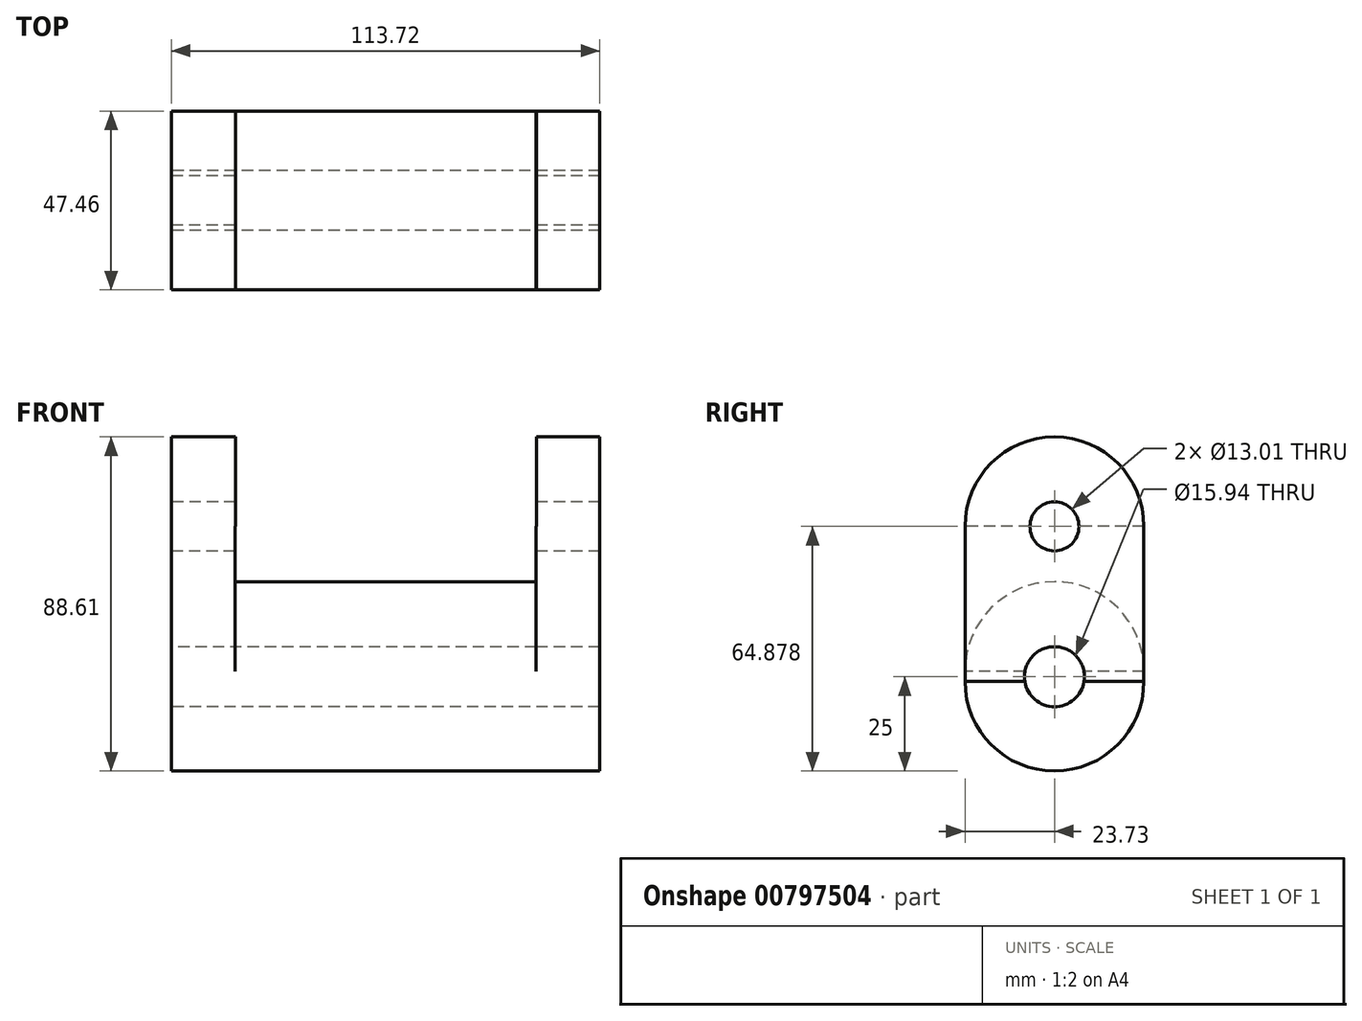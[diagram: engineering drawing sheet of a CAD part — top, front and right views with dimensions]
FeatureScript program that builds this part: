
annotation { "Feature Type Name" : "Feature", "Feature Type Description" : "" }
export const myFeature = defineFeature(function(context is Context, id is Id, definition is map)
    precondition{}
    {
        {
            var Q0;
            Q0=qCreatedBy(makeId("Top.planeOp"),FACE);
            var sketch = newSketch(context, id + "F0", { "sketchPlane" : qUnion([Q0])});
            skLineSegment(sketch, "E0.bottom", {"start": v(39.5, 23.73) * mm, "end": v(-39.5, 23.73) * mm});
            skLineSegment(sketch, "E0.top", {"start": v(39.5, -23.73) * mm, "end": v(-39.5, -23.73) * mm});
            skLineSegment(sketch, "E0.left", {"start": v(39.5, 23.73) * mm, "end": v(39.5, -23.73) * mm});
            skLineSegment(sketch, "E0.right", {"start": v(-39.5, 23.73) * mm, "end": v(-39.5, -23.73) * mm});
            skPoint(sketch, "E0.middle", {"position": v(0, 0) * mm});
            skLineSegment(sketch, "E1.bottom", {"start": v(-39.5, 0) * mm, "end": v(-56.86, 0) * mm});
            skLineSegment(sketch, "E1.top", {"start": v(-39.5, 23.73) * mm, "end": v(-56.86, 23.73) * mm});
            skLineSegment(sketch, "E1.left", {"start": v(-39.5, 0) * mm, "end": v(-39.5, 23.73) * mm});
            skLineSegment(sketch, "E1.right", {"start": v(-56.86, 0) * mm, "end": v(-56.86, 23.73) * mm});
            skLineSegment(sketch, "E2.bottom", {"start": v(-56.86, 0) * mm, "end": v(-39.5, 0) * mm});
            skLineSegment(sketch, "E2.top", {"start": v(-56.86, -23.73) * mm, "end": v(-39.5, -23.73) * mm});
            skLineSegment(sketch, "E2.left", {"start": v(-56.86, 0) * mm, "end": v(-56.86, -23.73) * mm});
            skLineSegment(sketch, "E2.right", {"start": v(-39.5, 0) * mm, "end": v(-39.5, -23.73) * mm});
            skLineSegment(sketch, "E3.bottom", {"start": v(39.5, 23.73) * mm, "end": v(56.86, 23.73) * mm});
            skLineSegment(sketch, "E3.top", {"start": v(39.5, 0) * mm, "end": v(56.86, 0) * mm});
            skLineSegment(sketch, "E3.left", {"start": v(39.5, 23.73) * mm, "end": v(39.5, 0) * mm});
            skLineSegment(sketch, "E3.right", {"start": v(56.86, 23.73) * mm, "end": v(56.86, 0) * mm});
            skLineSegment(sketch, "E4.bottom", {"start": v(56.86, 0) * mm, "end": v(39.5, 0) * mm});
            skLineSegment(sketch, "E4.top", {"start": v(56.86, -23.73) * mm, "end": v(39.5, -23.73) * mm});
            skLineSegment(sketch, "E4.left", {"start": v(56.86, 0) * mm, "end": v(56.86, -23.73) * mm});
            skLineSegment(sketch, "E4.right", {"start": v(39.5, 0) * mm, "end": v(39.5, -23.73) * mm});
            skSolve(sketch);
        }
        {
            var Q0;
            {var subQ2=sQuery(id+"F0.wireOp",EDGE,"E1.bottom");Q0=makeQuery(id+"F0.imprint","IMPRINT",FACE,{"disambiguationData":[TD([[makeQuery(id+"F0.imprint","IMPRINT",EDGE,{"derivedFrom":subQ2}),-1.0]])]});}
            var Q1;
            {var subQ2=sQuery(id+"F0.wireOp",EDGE,"E1.bottom");Q1=makeQuery(id+"F0.imprint","IMPRINT",FACE,{"disambiguationData":[TD([[makeQuery(id+"F0.imprint","IMPRINT",EDGE,{"derivedFrom":subQ2}),1.0]])]});}
            var Q2;
            {var subQ1=sQuery(id+"F0.wireOp",EDGE,"E0.bottom");Q2=makeQuery(id+"F0.imprint","IMPRINT",FACE,{"disambiguationData":[TD([[makeQuery(id+"F0.imprint","IMPRINT",EDGE,{"derivedFrom":subQ1}),1.0]])]});}
            var Q3;
            {var subQ0=sQuery(id+"F0.wireOp",EDGE,"E3.bottom");Q3=makeQuery(id+"F0.imprint","IMPRINT",FACE,{"disambiguationData":[TD([[makeQuery(id+"F0.imprint","IMPRINT",EDGE,{"derivedFrom":subQ0}),-1.0]])]});}
            var Q4;
            {var subQ2=sQuery(id+"F0.wireOp",EDGE,"E3.top");Q4=makeQuery(id+"F0.imprint","IMPRINT",FACE,{"disambiguationData":[TD([[makeQuery(id+"F0.imprint","IMPRINT",EDGE,{"derivedFrom":subQ2}),-1.0]])]});}
            extrude(context, id + "F1", {"entities" : qUnion([Q0, Q1, Q2, Q3, Q4]), "oppositeDirection" : true, "depth" : 1.27 * mm, "offsetDistance" : 25.4 * mm});
        }
        {
            var Q0;
            Q0=makeQuery(id+"F1.opExtrude","SWEPT_FACE",FACE,{"disambiguationData":[OSD([sQuery(id+"F0.wireOp",EDGE,"E1.right"),sQuery(id+"F0.wireOp",EDGE,"E2.left")])]});
            var sketch = newSketch(context, id + "F2", { "sketchPlane" : qUnion([Q0])});
            skArc(sketch, "E5", {"start": v(-23.73, -1.27) * mm, "mid": v(0, -25) * mm, "end": v(23.73, -1.27) * mm});
            skSolve(sketch);
        }
        {
            var Q0;
            Q0 = qSketchRegion(id + "F2", true);
            var Q1;
            Q1=makeQuery(id+"F2.imprint","IMPRINT",FACE,{"disambiguationData":[TD([[makeQuery(id+"F2.imprint","IMPRINT",EDGE,{"derivedFrom":sQuery(id+"F2.wireOp",EDGE,"E5")}),1.0]])]});
            extrude(context, id + "F3", {"entities" : qUnion([Q0, Q1]), "operationType" : NewBodyOperationType.ADD, "oppositeDirection" : true, "depth" : 113.7 * mm, "offsetDistance" : 25.4 * mm});
        }
        {
            var Q0;
            Q0=makeQuery(id+"F1.opExtrude","CAP_FACE",FACE,{"disambiguationData":[OSD([sQuery(id+"F0.wireOp",EDGE,"E0.bottom"),sQuery(id+"F0.wireOp",EDGE,"E0.top"),sQuery(id+"F0.wireOp",EDGE,"E1.top"),sQuery(id+"F0.wireOp",EDGE,"E1.right"),sQuery(id+"F0.wireOp",EDGE,"E2.top"),sQuery(id+"F0.wireOp",EDGE,"E2.left"),sQuery(id+"F0.wireOp",EDGE,"E3.bottom"),sQuery(id+"F0.wireOp",EDGE,"E3.right"),sQuery(id+"F0.wireOp",EDGE,"E4.top"),sQuery(id+"F0.wireOp",EDGE,"E4.left")])],"isStart":true});
            var sketch = newSketch(context, id + "F4", { "sketchPlane" : qUnion([Q0])});
            skLineSegment(sketch, "E6.bottom", {"start": v(39.97, 23.73) * mm, "end": v(-39.97, 23.73) * mm});
            skLineSegment(sketch, "E6.top", {"start": v(39.97, -23.73) * mm, "end": v(-39.97, -23.73) * mm});
            skLineSegment(sketch, "E6.left", {"start": v(39.97, 23.73) * mm, "end": v(39.97, -23.73) * mm});
            skLineSegment(sketch, "E6.right", {"start": v(-39.97, 23.73) * mm, "end": v(-39.97, -23.73) * mm});
            skPoint(sketch, "E6.middle", {"position": v(0, 0) * mm});
            skSolve(sketch);
        }
        {
            var Q0;
            Q0=makeQuery(id+"F4.imprint","IMPRINT",FACE,{"disambiguationData":[TD([[makeQuery(id+"F4.imprint","IMPRINT",EDGE,{"derivedFrom":sQuery(id+"F4.wireOp",EDGE,"E6.bottom")}),1.0]])]});
            extrude(context, id + "F5", {"entities" : qUnion([Q0]), "operationType" : NewBodyOperationType.ADD, "depth" : 1.5 * mm, "offsetDistance" : 25.4 * mm});
        }
        {
            var Q0;
            Q0=makeQuery(id+"F5.opExtrude","SWEPT_FACE",FACE,{"disambiguationData":[OSD([sQuery(id+"F4.wireOp",EDGE,"E6.right")])]});
            var sketch = newSketch(context, id + "F6", { "sketchPlane" : qUnion([Q0])});
            skArc(sketch, "E7", {"start": v(23.73, 1.5) * mm, "mid": v(0, 25.23) * mm, "end": v(-23.73, 1.5) * mm});
            skSolve(sketch);
        }
        {
            var Q0;
            Q0 = qSketchRegion(id + "F6", true);
            var Q1;
            Q1=makeQuery(id+"F6.imprint","IMPRINT",FACE,{"disambiguationData":[TD([[makeQuery(id+"F6.imprint","IMPRINT",EDGE,{"derivedFrom":sQuery(id+"F6.wireOp",EDGE,"E7")}),1.0]])]});
            extrude(context, id + "F7", {"entities" : qUnion([Q0, Q1]), "operationType" : NewBodyOperationType.ADD, "oppositeDirection" : true, "depth" : 79.93 * mm, "offsetDistance" : 25.4 * mm});
        }
        {
            var Q0;
            {var subQ0=sQuery(id+"F0.wireOp",EDGE,"E2.left");var subQ1=sQuery(id+"F0.wireOp",EDGE,"E1.right");var subQ2=sQuery(id+"F0.wireOp",EDGE,"E3.bottom");var subQ3=sQuery(id+"F0.wireOp",EDGE,"E1.top");var subQ4=sQuery(id+"F0.wireOp",EDGE,"E0.bottom");var subQ5=sQuery(id+"F0.wireOp",EDGE,"E4.top");var subQ6=sQuery(id+"F0.wireOp",EDGE,"E2.top");var subQ7=sQuery(id+"F0.wireOp",EDGE,"E0.top");Q0=makeQuery(id+"F5.boolean.opBoolean","SPLIT",FACE,{"disambiguationData":[TD([makeQuery(id+"F5.opExtrude","SWEPT_FACE",FACE,{"disambiguationData":[OSD([sQuery(id+"F4.wireOp",EDGE,"E6.right")])]})])],"derivedFrom":makeQuery(id+"F1.opExtrude","CAP_FACE",FACE,{"disambiguationData":[OSD([subQ4,subQ7,subQ3,subQ1,subQ6,subQ0,subQ2,sQuery(id+"F0.wireOp",EDGE,"E3.right"),subQ5,sQuery(id+"F0.wireOp",EDGE,"E4.left")])],"isStart":true})});}
            var Q1;
            {var subQ0=sQuery(id+"F0.wireOp",EDGE,"E4.left");var subQ1=sQuery(id+"F0.wireOp",EDGE,"E3.right");var subQ2=sQuery(id+"F0.wireOp",EDGE,"E4.top");var subQ3=sQuery(id+"F0.wireOp",EDGE,"E2.top");var subQ4=sQuery(id+"F0.wireOp",EDGE,"E0.top");var subQ5=sQuery(id+"F0.wireOp",EDGE,"E3.bottom");var subQ6=sQuery(id+"F0.wireOp",EDGE,"E1.top");var subQ7=sQuery(id+"F0.wireOp",EDGE,"E0.bottom");Q1=makeQuery(id+"F5.boolean.opBoolean","SPLIT",FACE,{"disambiguationData":[TD([makeQuery(id+"F5.opExtrude","SWEPT_FACE",FACE,{"disambiguationData":[OSD([sQuery(id+"F4.wireOp",EDGE,"E6.left")])]})])],"derivedFrom":makeQuery(id+"F1.opExtrude","CAP_FACE",FACE,{"disambiguationData":[OSD([subQ7,subQ4,subQ6,sQuery(id+"F0.wireOp",EDGE,"E1.right"),subQ3,sQuery(id+"F0.wireOp",EDGE,"E2.left"),subQ5,subQ1,subQ2,subQ0])],"isStart":true})});}
            extrude(context, id + "F8", {"entities" : qUnion([Q0, Q1]), "operationType" : NewBodyOperationType.ADD, "depth" : 39.88 * mm, "offsetDistance" : 25.4 * mm});
        }
        {
            var Q0;
            {var subQ0=sQuery(id+"F0.wireOp",EDGE,"E2.left");var subQ1=sQuery(id+"F0.wireOp",EDGE,"E1.right");Q0=makeQuery(id+"F8.boolean.opBoolean","MERGE",FACE,{"derivedFrom":[makeQuery(id+"F3.boolean.opBoolean","MERGE",FACE,{"derivedFrom":[makeQuery(id+"F1.opExtrude","SWEPT_FACE",FACE,{"disambiguationData":[OSD([subQ1,subQ0])]}),makeQuery(id+"F3.opExtrude","CAP_FACE",FACE,{"disambiguationData":[OSD([subQ1,subQ0,sQuery(id+"F2.wireOp",EDGE,"E5")])],"isStart":true})]}),makeQuery(id+"F8.opExtrude","SWEPT_FACE",FACE,{"disambiguationData":[OSD([subQ1,subQ0])]})]});}
            var sketch = newSketch(context, id + "F9", { "sketchPlane" : qUnion([Q0])});
            skArc(sketch, "E8", {"start": v(23.73, 39.88) * mm, "mid": v(0, 63.6) * mm, "end": v(-23.73, 39.88) * mm});
            skSolve(sketch);
        }
        {
            var Q0;
            Q0=makeQuery(id+"F9.imprint","IMPRINT",FACE,{"disambiguationData":[TD([[makeQuery(id+"F9.imprint","IMPRINT",EDGE,{"derivedFrom":sQuery(id+"F9.wireOp",EDGE,"E8")}),1.0]])]});
            extrude(context, id + "F10", {"entities" : qUnion([Q0]), "operationType" : NewBodyOperationType.ADD, "oppositeDirection" : true, "depth" : 17.02 * mm, "offsetDistance" : 25.4 * mm});
        }
        {
            var Q0;
            {var subQ0=sQuery(id+"F0.wireOp",EDGE,"E4.left");var subQ1=sQuery(id+"F0.wireOp",EDGE,"E3.right");Q0=makeQuery(id+"F8.boolean.opBoolean","MERGE",FACE,{"derivedFrom":[makeQuery(id+"F1.opExtrude","SWEPT_FACE",FACE,{"disambiguationData":[OSD([subQ1,subQ0])]}),makeQuery(id+"F8.opExtrude","SWEPT_FACE",FACE,{"disambiguationData":[OSD([subQ1,subQ0])]})]});}
            var sketch = newSketch(context, id + "F11", { "sketchPlane" : qUnion([Q0])});
            skArc(sketch, "E9", {"start": v(23.73, 39.88) * mm, "mid": v(0, 63.6) * mm, "end": v(-23.73, 39.88) * mm});
            skSolve(sketch);
        }
        {
            var Q0;
            Q0 = qSketchRegion(id + "F11", true);
            var Q1;
            Q1=makeQuery(id+"F11.imprint","IMPRINT",FACE,{"disambiguationData":[TD([[makeQuery(id+"F11.imprint","IMPRINT",EDGE,{"derivedFrom":sQuery(id+"F11.wireOp",EDGE,"E9")}),1.0]])]});
            extrude(context, id + "F12", {"entities" : qUnion([Q0, Q1]), "operationType" : NewBodyOperationType.ADD, "oppositeDirection" : true, "depth" : 16.84 * mm, "offsetDistance" : 25.4 * mm});
        }
        {
            var Q0;
            {var subQ0=sQuery(id+"F0.wireOp",EDGE,"E2.left");var subQ1=sQuery(id+"F0.wireOp",EDGE,"E1.right");Q0=makeQuery(id+"F10.boolean.opBoolean","MERGE",FACE,{"derivedFrom":[makeQuery(id+"F8.boolean.opBoolean","MERGE",FACE,{"derivedFrom":[makeQuery(id+"F3.boolean.opBoolean","MERGE",FACE,{"derivedFrom":[makeQuery(id+"F1.opExtrude","SWEPT_FACE",FACE,{"disambiguationData":[OSD([subQ1,subQ0])]}),makeQuery(id+"F3.opExtrude","CAP_FACE",FACE,{"disambiguationData":[OSD([subQ1,subQ0,sQuery(id+"F2.wireOp",EDGE,"E5")])],"isStart":true})]}),makeQuery(id+"F8.opExtrude","SWEPT_FACE",FACE,{"disambiguationData":[OSD([subQ1,subQ0])]})]}),makeQuery(id+"F10.opExtrude","CAP_FACE",FACE,{"disambiguationData":[OSD([subQ1,subQ0,sQuery(id+"F9.wireOp",EDGE,"E8")])],"isStart":true})]});}
            var sketch = newSketch(context, id + "F13", { "sketchPlane" : qUnion([Q0])});
            skCircle(sketch, "E10", {"center": v(0, 39.88) * mm, "radius": 6.5 * mm});
            skSolve(sketch);
        }
        {
            var Q0;
            Q0 = qSketchRegion(id + "F13", true);
            extrude(context, id + "F14", {"entities" : qUnion([Q0]), "operationType" : NewBodyOperationType.REMOVE, "oppositeDirection" : true, "depth" : 198.63 * mm, "offsetDistance" : 25.4 * mm});
        }
        {
            var Q0;
            {var subQ0=sQuery(id+"F0.wireOp",EDGE,"E2.left");var subQ1=sQuery(id+"F0.wireOp",EDGE,"E1.right");Q0=makeQuery(id+"F10.boolean.opBoolean","MERGE",FACE,{"derivedFrom":[makeQuery(id+"F8.boolean.opBoolean","MERGE",FACE,{"derivedFrom":[makeQuery(id+"F3.boolean.opBoolean","MERGE",FACE,{"derivedFrom":[makeQuery(id+"F1.opExtrude","SWEPT_FACE",FACE,{"disambiguationData":[OSD([subQ1,subQ0])]}),makeQuery(id+"F3.opExtrude","CAP_FACE",FACE,{"disambiguationData":[OSD([subQ1,subQ0,sQuery(id+"F2.wireOp",EDGE,"E5")])],"isStart":true})]}),makeQuery(id+"F8.opExtrude","SWEPT_FACE",FACE,{"disambiguationData":[OSD([subQ1,subQ0])]})]}),makeQuery(id+"F10.opExtrude","CAP_FACE",FACE,{"disambiguationData":[OSD([subQ1,subQ0,sQuery(id+"F9.wireOp",EDGE,"E8")])],"isStart":true})]});}
            var sketch = newSketch(context, id + "F15", { "sketchPlane" : qUnion([Q0])});
            skCircle(sketch, "E11", {"center": v(0, 0) * mm, "radius": 7.97 * mm});
            skSolve(sketch);
        }
        {
            var Q0;
            Q0=makeQuery(id+"F15.imprint","IMPRINT",FACE,{"disambiguationData":[TD([[makeQuery(id+"F15.imprint","IMPRINT",EDGE,{"derivedFrom":sQuery(id+"F15.wireOp",EDGE,"E11")}),1.0]])]});
            extrude(context, id + "F16", {"entities" : qUnion([Q0]), "operationType" : NewBodyOperationType.REMOVE, "oppositeDirection" : true, "depth" : 343.92 * mm, "offsetDistance" : 25.4 * mm});
        }
    });
